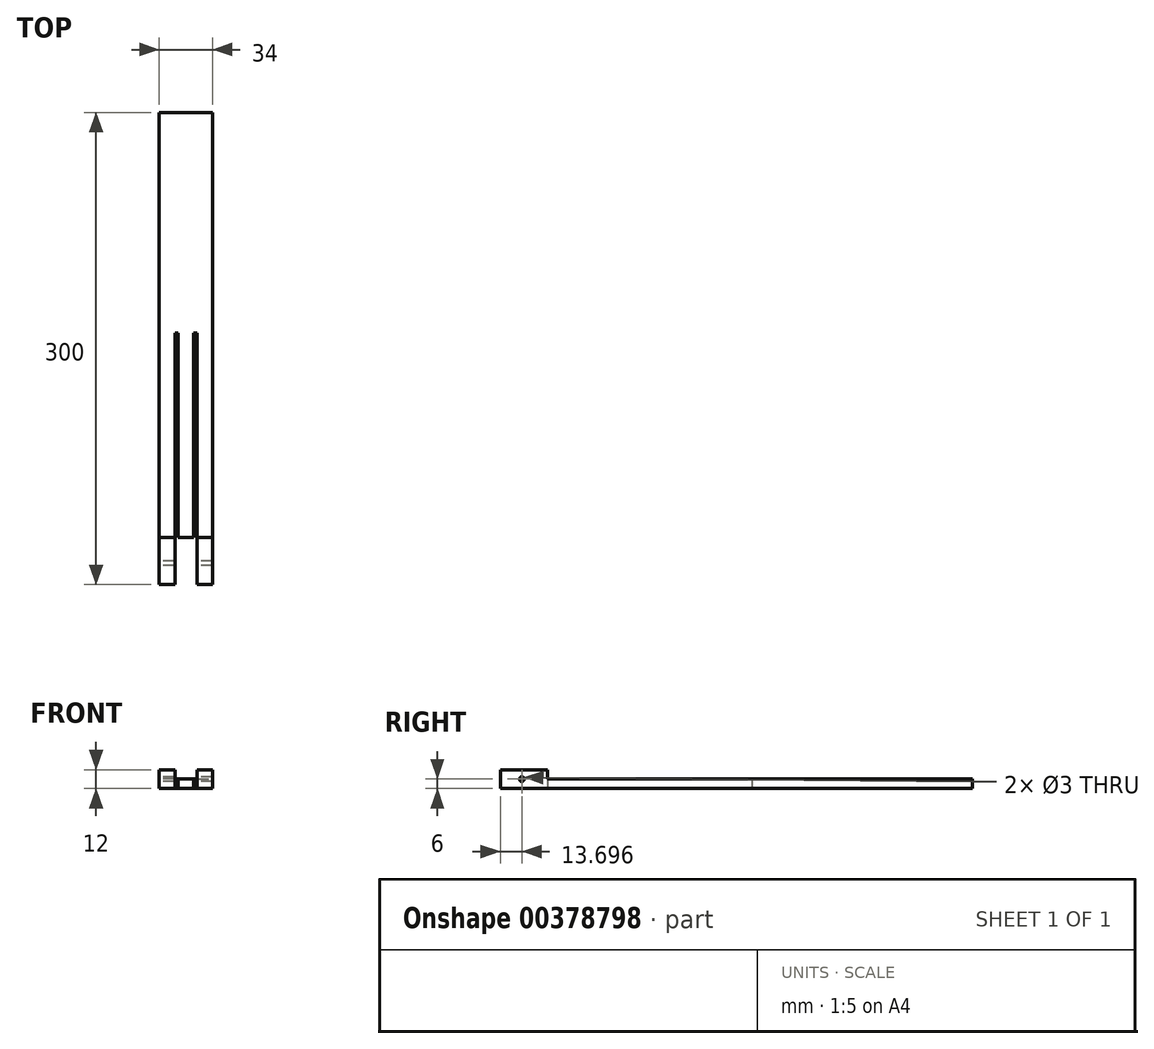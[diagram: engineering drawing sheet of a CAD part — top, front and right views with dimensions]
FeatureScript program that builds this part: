
annotation { "Feature Type Name" : "Feature", "Feature Type Description" : "" }
export const myFeature = defineFeature(function(context is Context, id is Id, definition is map)
    precondition{}
    {
        {
            var Q0;
            Q0=qCreatedBy(makeId("Top.planeOp"),FACE);
            var sketch = newSketch(context, id + "F0", { "sketchPlane" : qUnion([Q0])});
            skLineSegment(sketch, "E0.bottom", {"start": v(17, -150) * mm, "end": v(7, -150) * mm});
            skLineSegment(sketch, "E0.top", {"start": v(17, 150) * mm, "end": v(-17, 150) * mm});
            skLineSegment(sketch, "E0.left", {"start": v(17, -150) * mm, "end": v(17, 150) * mm});
            skLineSegment(sketch, "E0.right", {"start": v(-17, -150) * mm, "end": v(-17, 150) * mm});
            skPoint(sketch, "E0.middle", {"position": v(0, 0) * mm});
            skLineSegment(sketch, "E1.top", {"start": v(-7, 10) * mm, "end": v(-5, 10) * mm});
            skLineSegment(sketch, "E1.left", {"start": v(-7, -150) * mm, "end": v(-7, 10) * mm});
            skLineSegment(sketch, "E1.right", {"start": v(-5, -120) * mm, "end": v(-5, 10) * mm});
            skLineSegment(sketch, "E2.top", {"start": v(5, 10) * mm, "end": v(7, 10) * mm});
            skLineSegment(sketch, "E2.left", {"start": v(5, -120) * mm, "end": v(5, 10) * mm});
            skLineSegment(sketch, "E2.right", {"start": v(7, -150) * mm, "end": v(7, 10) * mm});
            skLineSegment(sketch, "E3.trimOffspring", {"start": v(-7, -150) * mm, "end": v(-17, -150) * mm});
            skLineSegment(sketch, "E4.top", {"start": v(-5, -120) * mm, "end": v(5, -120) * mm});
            skSolve(sketch);
        }
        {
            var Q0;
            Q0=makeQuery(id+"F0.imprint","IMPRINT",FACE,{"disambiguationData":[TD([[makeQuery(id+"F0.imprint","IMPRINT",EDGE,{"derivedFrom":sQuery(id+"F0.wireOp",EDGE,"E0.bottom")}),-1.0]])]});
            extrude(context, id + "F1", {"entities" : qUnion([Q0]), "depth" : 6 * mm});
        }
        {
            var Q0;
            Q0=makeQuery(id+"F1.opExtrude","CAP_FACE",FACE,{"disambiguationData":[OSD([sQuery(id+"F0.wireOp",EDGE,"E0.bottom"),sQuery(id+"F0.wireOp",EDGE,"E0.top"),sQuery(id+"F0.wireOp",EDGE,"E0.left"),sQuery(id+"F0.wireOp",EDGE,"E0.right"),sQuery(id+"F0.wireOp",EDGE,"E1.top"),sQuery(id+"F0.wireOp",EDGE,"E1.left"),sQuery(id+"F0.wireOp",EDGE,"E1.right"),sQuery(id+"F0.wireOp",EDGE,"E2.top"),sQuery(id+"F0.wireOp",EDGE,"E2.left"),sQuery(id+"F0.wireOp",EDGE,"E2.right"),sQuery(id+"F0.wireOp",EDGE,"E3.trimOffspring"),sQuery(id+"F0.wireOp",EDGE,"E4.top")])],"isStart":false});
            var sketch = newSketch(context, id + "F2", { "sketchPlane" : qUnion([Q0])});
            skLineSegment(sketch, "E5.bottom", {"start": v(-7, -120) * mm, "end": v(-17, -120) * mm});
            skLineSegment(sketch, "E5.top", {"start": v(-7, -150) * mm, "end": v(-17, -150) * mm});
            skLineSegment(sketch, "E5.left", {"start": v(-7, -120) * mm, "end": v(-7, -150) * mm});
            skLineSegment(sketch, "E5.right", {"start": v(-17, -120) * mm, "end": v(-17, -150) * mm});
            skLineSegment(sketch, "E6.bottom", {"start": v(7, -120) * mm, "end": v(17, -120) * mm});
            skLineSegment(sketch, "E6.top", {"start": v(7, -150) * mm, "end": v(17, -150) * mm});
            skLineSegment(sketch, "E6.left", {"start": v(7, -120) * mm, "end": v(7, -150) * mm});
            skLineSegment(sketch, "E6.right", {"start": v(17, -120) * mm, "end": v(17, -150) * mm});
            skSolve(sketch);
        }
        {
            var Q0;
            Q0=makeQuery(id+"F2.imprint","IMPRINT",FACE,{"disambiguationData":[TD([[makeQuery(id+"F2.imprint","IMPRINT",EDGE,{"derivedFrom":sQuery(id+"F2.wireOp",EDGE,"E5.bottom")}),1.0]])]});
            var Q1;
            Q1=makeQuery(id+"F2.imprint","IMPRINT",FACE,{"disambiguationData":[TD([[makeQuery(id+"F2.imprint","IMPRINT",EDGE,{"derivedFrom":sQuery(id+"F2.wireOp",EDGE,"E6.bottom")}),-1.0]])]});
            extrude(context, id + "F3", {"entities" : qUnion([Q0, Q1]), "operationType" : NewBodyOperationType.ADD, "depth" : 6 * mm});
        }
        {
            var Q0;
            Q0=makeQuery(id+"F3.boolean.opBoolean","MERGE",FACE,{"derivedFrom":[makeQuery(id+"F1.opExtrude","SWEPT_FACE",FACE,{"disambiguationData":[OSD([sQuery(id+"F0.wireOp",EDGE,"E0.right")])]}),makeQuery(id+"F3.opExtrude","SWEPT_FACE",FACE,{"disambiguationData":[OSD([sQuery(id+"F2.wireOp",EDGE,"E5.right")])]})]});
            var sketch = newSketch(context, id + "F4", { "sketchPlane" : qUnion([Q0])});
            skCircle(sketch, "E7", {"center": v(136.3, 6) * mm, "radius": 1.5 * mm});
            skPoint(sketch, "E7.centerSnap0", {"position": v(150, 6) * mm});
            skSolve(sketch);
        }
        {
            var Q0;
            Q0=makeQuery(id+"F4.imprint","IMPRINT",FACE,{"disambiguationData":[TD([[makeQuery(id+"F4.imprint","IMPRINT",EDGE,{"derivedFrom":sQuery(id+"F4.wireOp",EDGE,"E7")}),1.0]])]});
            extrude(context, id + "F5", {"entities" : qUnion([Q0]), "operationType" : NewBodyOperationType.REMOVE, "endBound" : BoundingType.THROUGH_ALL, "oppositeDirection" : true, "depth" : 25 * mm});
        }
    });
